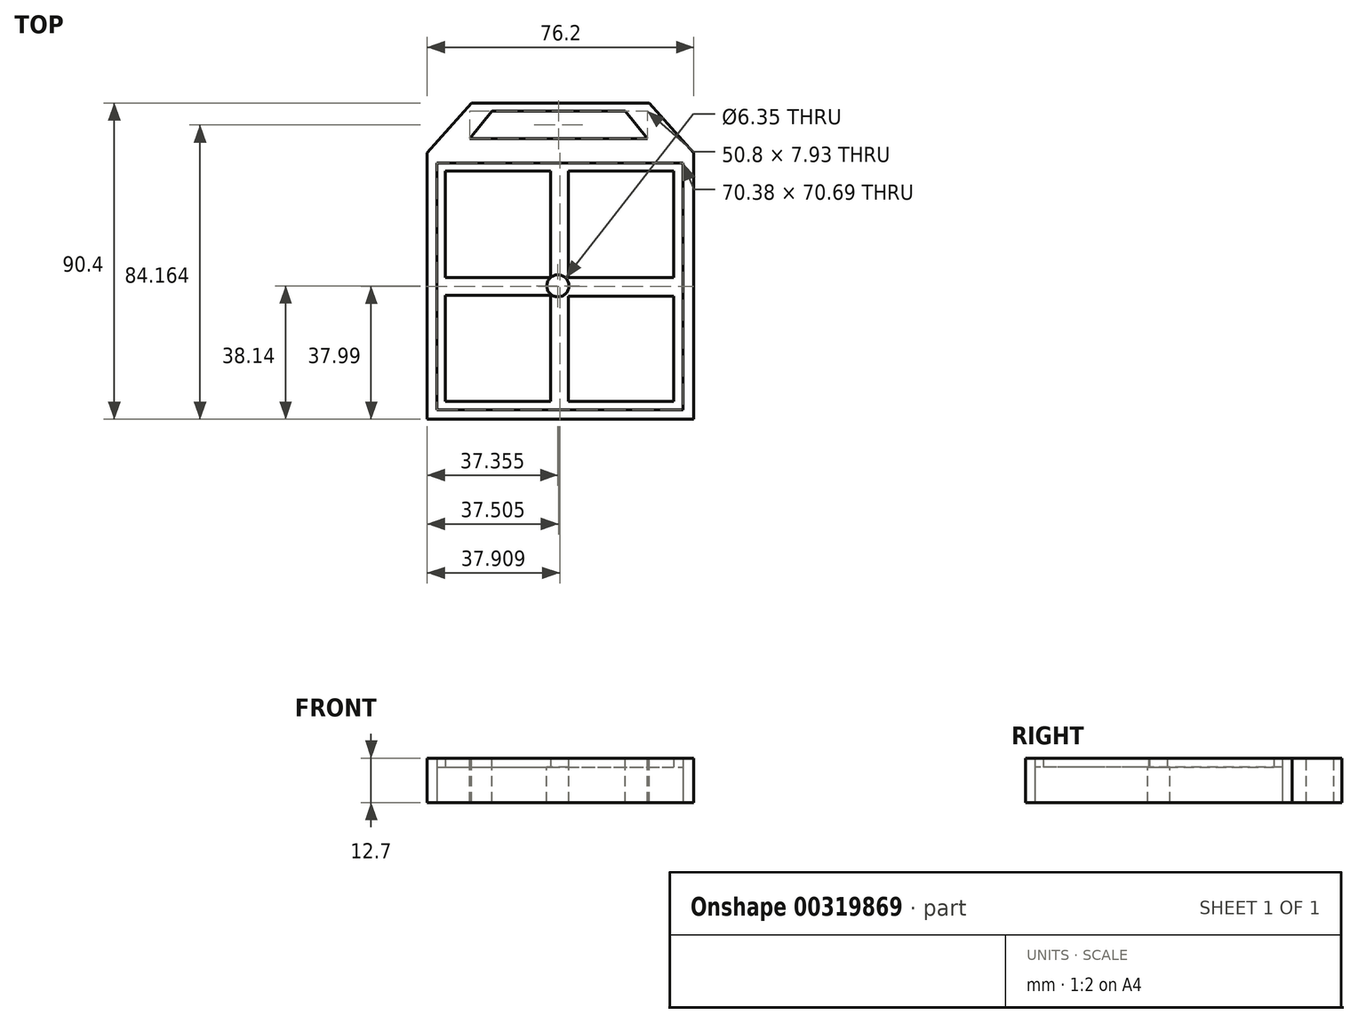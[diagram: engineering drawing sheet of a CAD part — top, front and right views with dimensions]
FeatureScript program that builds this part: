
annotation { "Feature Type Name" : "Feature", "Feature Type Description" : "" }
export const myFeature = defineFeature(function(context is Context, id is Id, definition is map)
    precondition{}
    {
        {
            var Q0;
            Q0=qCreatedBy(makeId("Top.planeOp"),FACE);
            var sketch = newSketch(context, id + "F0", { "sketchPlane" : qUnion([Q0])});
            skLineSegment(sketch, "E0", {"start": v(-108.6, 38.06) * mm, "end": v(-108.6, -38.14) * mm});
            skLineSegment(sketch, "E1", {"start": v(-108.6, -38.14) * mm, "end": v(-32.4, -38.14) * mm});
            skLineSegment(sketch, "E2", {"start": v(-32.4, -38.14) * mm, "end": v(-32.4, 38.06) * mm});
            skLineSegment(sketch, "E3", {"start": v(-32.4, 38.06) * mm, "end": v(-108.6, 38.06) * mm});
            skPoint(sketch, "E4.end.orphan", {"position": v(-70.5, -57.45) * mm});
            skLineSegment(sketch, "E5.bottom", {"start": v(-105.88, 35.2) * mm, "end": v(-35.5, 35.2) * mm});
            skLineSegment(sketch, "E5.top", {"start": v(-105.88, -35.5) * mm, "end": v(-35.5, -35.5) * mm});
            skLineSegment(sketch, "E5.left", {"start": v(-105.88, 35.2) * mm, "end": v(-105.88, -35.5) * mm});
            skLineSegment(sketch, "E5.right", {"start": v(-35.5, 35.2) * mm, "end": v(-35.5, -35.5) * mm});
            skSolve(sketch);
        }
        {
            var Q0;
            Q0 = qSketchRegion(id + "F0", true);
            extrude(context, id + "F1", {"entities" : qUnion([Q0]), "depth" : 12.7 * mm});
        }
        {
            var Q0;
            Q0=makeQuery(id+"F0.imprint","IMPRINT",FACE,{"disambiguationData":[TD([[makeQuery(id+"F0.imprint","IMPRINT",EDGE,{"derivedFrom":sQuery(id+"F0.wireOp",EDGE,"E5.bottom")}),-1.0]])]});
            extrude(context, id + "F2", {"entities" : qUnion([Q0]), "depth" : 10.16 * mm});
        }
        {
            var Q0;
            Q0=makeQuery(id+"F2.opExtrude","CAP_FACE",FACE,{"disambiguationData":[OSD([sQuery(id+"F0.wireOp",EDGE,"E5.bottom"),sQuery(id+"F0.wireOp",EDGE,"E5.top"),sQuery(id+"F0.wireOp",EDGE,"E5.left"),sQuery(id+"F0.wireOp",EDGE,"E5.right")])],"isStart":false});
            var sketch = newSketch(context, id + "F3", { "sketchPlane" : qUnion([Q0])});
            skLineSegment(sketch, "E6", {"start": v(-105.88, -0.15) * mm, "end": v(-35.5, -0.15) * mm});
            skLineSegment(sketch, "E7", {"start": v(-70.7, 35.2) * mm, "end": v(-70.7, -35.5) * mm});
            skLineSegment(sketch, "E8.bottom", {"start": v(-103.43, 32.79) * mm, "end": v(-73.35, 32.79) * mm});
            skLineSegment(sketch, "E8.top", {"start": v(-103.43, 2.4) * mm, "end": v(-73.35, 2.4) * mm});
            skLineSegment(sketch, "E8.left", {"start": v(-103.43, 32.79) * mm, "end": v(-103.43, 2.4) * mm});
            skLineSegment(sketch, "E8.right", {"start": v(-73.35, 32.79) * mm, "end": v(-73.35, 2.4) * mm});
            skLineSegment(sketch, "E9.bottom", {"start": v(-103.43, -2.7) * mm, "end": v(-73.35, -2.7) * mm});
            skLineSegment(sketch, "E9.top", {"start": v(-103.43, -33.09) * mm, "end": v(-73.35, -33.09) * mm});
            skLineSegment(sketch, "E9.left", {"start": v(-103.43, -2.7) * mm, "end": v(-103.43, -33.09) * mm});
            skLineSegment(sketch, "E9.right", {"start": v(-73.35, -2.7) * mm, "end": v(-73.35, -33.09) * mm});
            skLineSegment(sketch, "E10.bottom", {"start": v(-68.24, -3) * mm, "end": v(-38.16, -3) * mm});
            skLineSegment(sketch, "E10.top", {"start": v(-68.24, -33.09) * mm, "end": v(-38.16, -33.09) * mm});
            skLineSegment(sketch, "E10.left", {"start": v(-68.24, -3) * mm, "end": v(-68.24, -33.09) * mm});
            skLineSegment(sketch, "E10.right", {"start": v(-38.16, -3) * mm, "end": v(-38.16, -33.09) * mm});
            skPoint(sketch, "E11.oppositeSnap0", {"position": v(-38.16, -18.05) * mm});
            skLineSegment(sketch, "E11.bottom", {"start": v(-68.24, 2.4) * mm, "end": v(-38.16, 2.4) * mm});
            skLineSegment(sketch, "E11.top", {"start": v(-68.24, 32.79) * mm, "end": v(-38.16, 32.79) * mm});
            skLineSegment(sketch, "E11.left", {"start": v(-68.24, 2.4) * mm, "end": v(-68.24, 32.79) * mm});
            skLineSegment(sketch, "E11.right", {"start": v(-38.16, 2.4) * mm, "end": v(-38.16, 32.79) * mm});
            skSolve(sketch);
        }
        {
            var Q0;
            Q0 = qSketchRegion(id + "F3", true);
            extrude(context, id + "F4", {"entities" : qUnion([Q0]), "operationType" : NewBodyOperationType.ADD, "depth" : 2.54 * mm});
        }
        {
            var Q0;
            Q0=makeQuery(id+"F2.opExtrude","CAP_FACE",FACE,{"disambiguationData":[OSD([sQuery(id+"F0.wireOp",EDGE,"E5.bottom"),sQuery(id+"F0.wireOp",EDGE,"E5.top"),sQuery(id+"F0.wireOp",EDGE,"E5.left"),sQuery(id+"F0.wireOp",EDGE,"E5.right")])],"isStart":false});
            var sketch = newSketch(context, id + "F5", { "sketchPlane" : qUnion([Q0])});
            skPoint(sketch, "E12", {"position": v(-71.24, 0) * mm});
            skSolve(sketch);
        }
        {
            var Q0;
            Q0=sQuery(id+"F5.wireOp",VERTEX,"E12");
            var Q1;
            Q1=makeQuery(id+"F2.opExtrude","SWEPT_BODY",BODY,{"disambiguationData":[OSD([sQuery(id+"F0.wireOp",EDGE,"E5.bottom"),sQuery(id+"F0.wireOp",EDGE,"E5.top"),sQuery(id+"F0.wireOp",EDGE,"E5.left"),sQuery(id+"F0.wireOp",EDGE,"E5.right")])]});
            hole(context, id + "F6", {"style" : HoleStyle.SIMPLE, "endStyle" : HoleEndStyle.THROUGH, "holeDiameter" : 6.35 * mm, "tappedDepth" : 12.7 * mm, "tapClearance" : 3, "locations" : qUnion([Q0]), "scope" : qUnion([Q1])});
        }
        {
            var Q0;
            Q0=makeQuery(id+"F1.opExtrude","CAP_FACE",FACE,{"disambiguationData":[OSD([sQuery(id+"F0.wireOp",EDGE,"E0"),sQuery(id+"F0.wireOp",EDGE,"E1"),sQuery(id+"F0.wireOp",EDGE,"E2"),sQuery(id+"F0.wireOp",EDGE,"E3"),sQuery(id+"F0.wireOp",EDGE,"E5.bottom"),sQuery(id+"F0.wireOp",EDGE,"E5.top"),sQuery(id+"F0.wireOp",EDGE,"E5.left"),sQuery(id+"F0.wireOp",EDGE,"E5.right")])],"isStart":false});
            var sketch = newSketch(context, id + "F7", { "sketchPlane" : qUnion([Q0])});
            skLineSegment(sketch, "E13", {"start": v(-108.6, 38.06) * mm, "end": v(-95.9, 52.26) * mm});
            skLineSegment(sketch, "E14", {"start": v(-95.9, 52.26) * mm, "end": v(-45.1, 52.26) * mm});
            skLineSegment(sketch, "E15", {"start": v(-45.1, 52.26) * mm, "end": v(-32.4, 38.06) * mm});
            skSolve(sketch);
        }
        {
            var Q0;
            Q0=makeQuery(id+"F7.imprint","IMPRINT",FACE,{"disambiguationData":[TD([[makeQuery(id+"F7.imprint","IMPRINT",EDGE,{"derivedFrom":sQuery(id+"F7.wireOp",EDGE,"E13")}),-1.0]])]});
            var sketch = newSketch(context, id + "F8", { "sketchPlane" : qUnion([Q0])});
            skLineSegment(sketch, "E16", {"start": v(-96.5, 42.06) * mm, "end": v(-45.7, 42.06) * mm});
            skLineSegment(sketch, "E17", {"start": v(-45.7, 42.06) * mm, "end": v(-52.04, 49.99) * mm});
            skLineSegment(sketch, "E18", {"start": v(-52.04, 49.99) * mm, "end": v(-90.14, 49.99) * mm});
            skLineSegment(sketch, "E19", {"start": v(-90.14, 49.99) * mm, "end": v(-96.5, 42.06) * mm});
            skSolve(sketch);
        }
        {
            var Q0;
            Q0=makeQuery(id+"F7.imprint","IMPRINT",FACE,{"disambiguationData":[TD([[makeQuery(id+"F7.imprint","IMPRINT",EDGE,{"derivedFrom":sQuery(id+"F7.wireOp",EDGE,"E13")}),-1.0]])]});
            extrude(context, id + "F9", {"entities" : qUnion([Q0]), "operationType" : NewBodyOperationType.ADD, "oppositeDirection" : true, "depth" : 12.7 * mm});
        }
        {
            var Q0;
            Q0=makeQuery(id+"F8.imprint","IMPRINT",FACE,{"disambiguationData":[TD([[makeQuery(id+"F8.imprint","IMPRINT",EDGE,{"derivedFrom":sQuery(id+"F8.wireOp",EDGE,"E16")}),1.0]])]});
            extrude(context, id + "F10", {"entities" : qUnion([Q0]), "operationType" : NewBodyOperationType.REMOVE, "endBound" : BoundingType.THROUGH_ALL, "oppositeDirection" : true, "depth" : 25.4 * mm});
        }
    });
